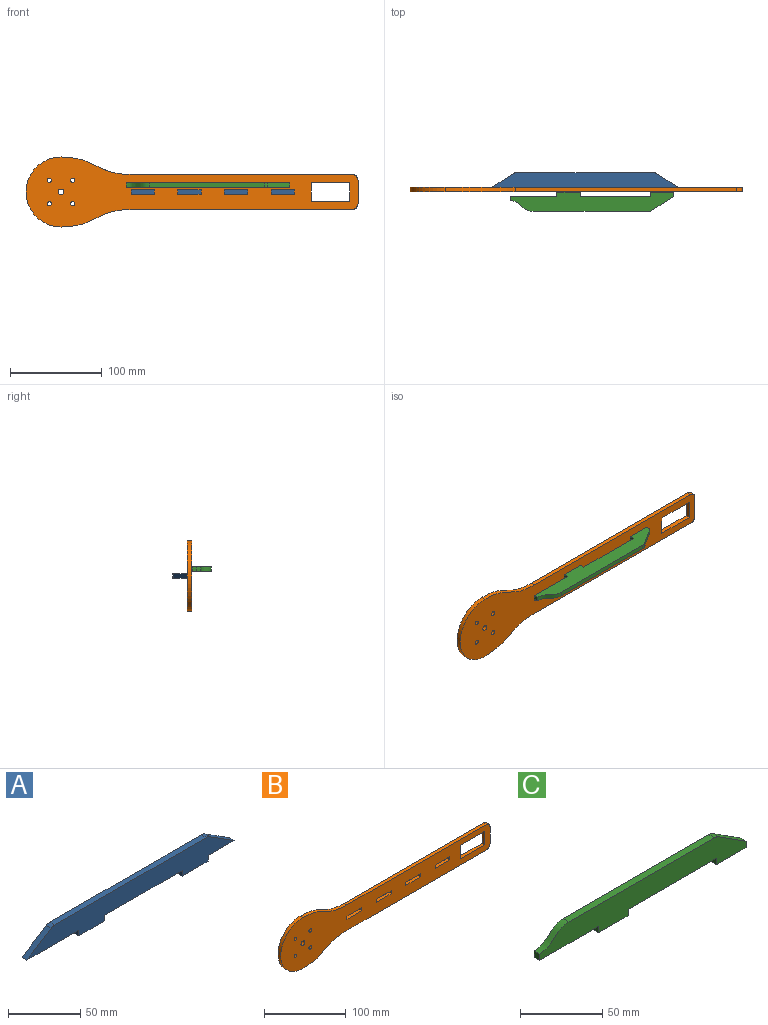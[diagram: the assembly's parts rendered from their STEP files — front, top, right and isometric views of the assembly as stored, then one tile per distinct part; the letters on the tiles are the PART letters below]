
ASSEMBLY  parts=3 mates=1
PART A: 16 faces, bbox 203.2x4.8x21 mm
  f0: plane 50.8x4.76mm, normal (0,0,-1), area 241.9mm2, adj f1,f13,f14,f15
  f1: plane 4.76x4.76mm, normal (-1,0,0), area 22.7mm2, adj f0,f2,f14,f15
  f2: plane 25.4x4.76mm, normal (0,0,-1), area 121mm2, adj f1,f3,f14,f15
  f3: plane 4.76x4.76mm, normal (1,0,0), area 22.7mm2, adj f2,f4,f14,f15
  f4: plane 76.2x4.76mm, normal (0,0,-1), area 362.9mm2, adj f3,f5,f14,f15
  f5: plane 4.76x4.76mm, normal (-1,0,0), area 22.7mm2, adj f4,f6,f14,f15
  f6: plane 25.4x4.76mm, normal (0,0,-1), area 121mm2, adj f5,f7,f14,f15
  f7: plane 4.76x4.76mm, normal (1,0,0), area 22.7mm2, adj f6,f8,f14,f15
  f8: plane 25.4x4.76mm, normal (0,0,-1), area 121mm2, adj f7,f9,f14,f15
  f9: plane 23.84x15.21mm, normal (0.54,0,0.84), area 134.7mm2, adj f8,f10,f14,f15
  f10: cylinder r=6.35mm len=4.76mm, axis (0,1,0), area 17.2mm2, adj f9,f11,f14,f15
  f11: plane 148.69x4.76mm, normal (0,0,1), area 708.2mm2, adj f10,f12,f14,f15
  f12: cylinder r=6.35mm len=4.76mm, axis (0,1,0), area 17.2mm2, adj f11,f13,f14,f15
  f13: plane 23.84x15.21mm, normal (-0.54,0,0.84), area 134.7mm2, adj f0,f12,f14,f15
  f14: plane 203.2x20.97mm, normal (0,-1,0), area 3122.6mm2, adj f0,f1,f2,f3,f4,f5,f6,f7
  f15: plane 203.2x20.97mm, normal (0,1,0), area 3122.6mm2, adj f0,f1,f2,f3,f4,f5,f6,f7
PART B: 35 faces, bbox 361.3x4.8x76.2 mm
  f0: plane 25.4x4.76mm, normal (0,0,1), area 121mm2, adj f1,f32,f33,f34
  f1: plane 4.76x4.76mm, normal (1,0,0), area 22.7mm2, adj f0,f2,f33,f34
  f2: plane 25.4x4.76mm, normal (0,0,-1), area 121mm2, adj f1,f32,f33,f34
  f3: plane 20.32x4.76mm, normal (-1,0,0), area 96.8mm2, adj f4,f22,f33,f34
  f4: plane 41.91x4.76mm, normal (0,0,1), area 199.6mm2, adj f3,f5,f33,f34
  f5: plane 20.32x4.76mm, normal (1,0,0), area 96.8mm2, adj f4,f22,f33,f34
  f6: plane 4.76x4.76mm, normal (1,0,0), area 22.7mm2, adj f7,f23,f33,f34
  f7: plane 25.4x4.76mm, normal (0,0,-1), area 121mm2, adj f6,f8,f33,f34
  f8: plane 4.76x4.76mm, normal (-1,0,0), area 22.7mm2, adj f7,f23,f33,f34
  f9: plane 4.76x4.76mm, normal (1,0,0), area 22.7mm2, adj f10,f24,f33,f34
  f10: plane 25.4x4.76mm, normal (0,0,-1), area 121mm2, adj f9,f11,f33,f34
  f11: plane 4.76x4.76mm, normal (-1,0,0), area 22.7mm2, adj f10,f24,f33,f34
  f12: plane 4.76x4.76mm, normal (1,0,0), area 22.7mm2, adj f13,f25,f33,f34
  f13: plane 25.4x4.76mm, normal (0,0,-1), area 121mm2, adj f12,f14,f33,f34
  f14: plane 4.76x4.76mm, normal (-1,0,0), area 22.7mm2, adj f13,f25,f33,f34
  f15: cylinder r=38.1mm len=76.2mm, axis (0,1,0), area 570mm2, adj f16,f28,f33,f34
  f16: extruded ~76.2x19.05mm, area 378.4mm2, adj f15,f17,f33,f34
  f17: plane 240.67x4.76mm, normal (0,0,-1), area 1146.2mm2, adj f16,f18,f33,f34
  f18: cylinder r=6.35mm len=6.35mm, axis (0,1,0), area 47.5mm2, adj f17,f19,f33,f34
  f19: plane 25.4x4.76mm, normal (1,0,0), area 121mm2, adj f18,f20,f33,f34
  f20: cylinder r=6.35mm len=6.35mm, axis (0,1,0), area 47.5mm2, adj f19,f21,f33,f34
  f21: plane 240.67x4.76mm, normal (0,0,1), area 1146.2mm2, adj f20,f28,f33,f34
  f22: plane 41.91x4.76mm, normal (0,0,-1), area 199.6mm2, adj f3,f5,f33,f34
  f23: plane 25.4x4.76mm, normal (0,0,1), area 121mm2, adj f6,f8,f33,f34
  f24: plane 25.4x4.76mm, normal (0,0,1), area 121mm2, adj f9,f11,f33,f34
  f25: plane 25.4x4.76mm, normal (0,0,1), area 121mm2, adj f12,f14,f33,f34
  f26: cylinder r=2.32mm len=4.76mm, axis (0,1,0), area 69.5mm2, adj f33,f34
  f27: cylinder r=2.32mm len=4.76mm, axis (0,1,0), area 69.5mm2, adj f33,f34
  f28: extruded ~76.2x19.05mm, area 378.4mm2, adj f15,f21,f33,f34
  f29: cylinder r=3.17mm len=6.35mm, axis (0,1,0), area 95mm2, adj f33,f34
  f30: cylinder r=2.32mm len=4.76mm, axis (0,1,0), area 69.5mm2, adj f33,f34
  f31: cylinder r=2.32mm len=4.76mm, axis (0,1,0), area 69.5mm2, adj f33,f34
  f32: plane 4.76x4.76mm, normal (-1,0,0), area 22.7mm2, adj f0,f2,f33,f34
  f33: plane 361.32x76.2mm, normal (0,-1,0), area 14594mm2, adj f0,f1,f2,f3,f4,f5,f6,f7
  f34: plane 361.32x76.2mm, normal (0,1,0), area 14594mm2, adj f0,f1,f2,f3,f4,f5,f6,f7
PART C: 15 faces, bbox 177.8x4.8x21 mm
  f0: plane 50.8x4.76mm, normal (0,0,-1), area 241.9mm2, adj f1,f12,f13,f14
  f1: plane 4.76x4.76mm, normal (-1,0,0), area 22.7mm2, adj f0,f2,f13,f14
  f2: plane 25.4x4.76mm, normal (0,0,-1), area 121mm2, adj f1,f3,f13,f14
  f3: plane 4.76x4.76mm, normal (1,0,0), area 22.7mm2, adj f2,f4,f13,f14
  f4: plane 76.2x4.76mm, normal (0,0,-1), area 362.9mm2, adj f3,f5,f13,f14
  f5: plane 4.76x4.76mm, normal (-1,0,0), area 22.7mm2, adj f4,f6,f13,f14
  f6: plane 25.4x4.76mm, normal (0,0,-1), area 121mm2, adj f5,f7,f13,f14
  f7: plane 4.76x4.76mm, normal (1,0,0), area 22.7mm2, adj f6,f8,f13,f14
  f8: plane 23.84x15.21mm, normal (0.54,0,0.84), area 134.7mm2, adj f7,f9,f13,f14
  f9: cylinder r=6.35mm len=4.76mm, axis (0,1,0), area 17.2mm2, adj f8,f10,f13,f14
  f10: plane 125.15x4.76mm, normal (0,0,1), area 596mm2, adj f9,f11,f13,f14
  f11: extruded ~25.4x11.44mm, area 136.6mm2, adj f10,f12,f13,f14
  f12: plane 4.76x4.76mm, normal (-1,0,0), area 22.7mm2, adj f0,f11,f13,f14
  f13: plane 177.8x20.97mm, normal (0,-1,0), area 2771.8mm2, adj f0,f1,f2,f3,f4,f5,f6,f7
  f14: plane 177.8x20.97mm, normal (0,1,0), area 2771.8mm2, adj f0,f1,f2,f3,f4,f5,f6,f7
PLACE A rot(axis=(0,0.71,0.71),180deg) t=(349.22,-144.55,-52.73)mm
PLACE B t=(95.22,-139.78,-55.11)mm
PLACE C rot(axis=(1,0,0),90deg) t=(166.18,-144.87,-45.14)mm
MATE fastened A.f7 <-> B.f1  axis (-1,0,0) through (171.42,-139.78,-52.73)mm
